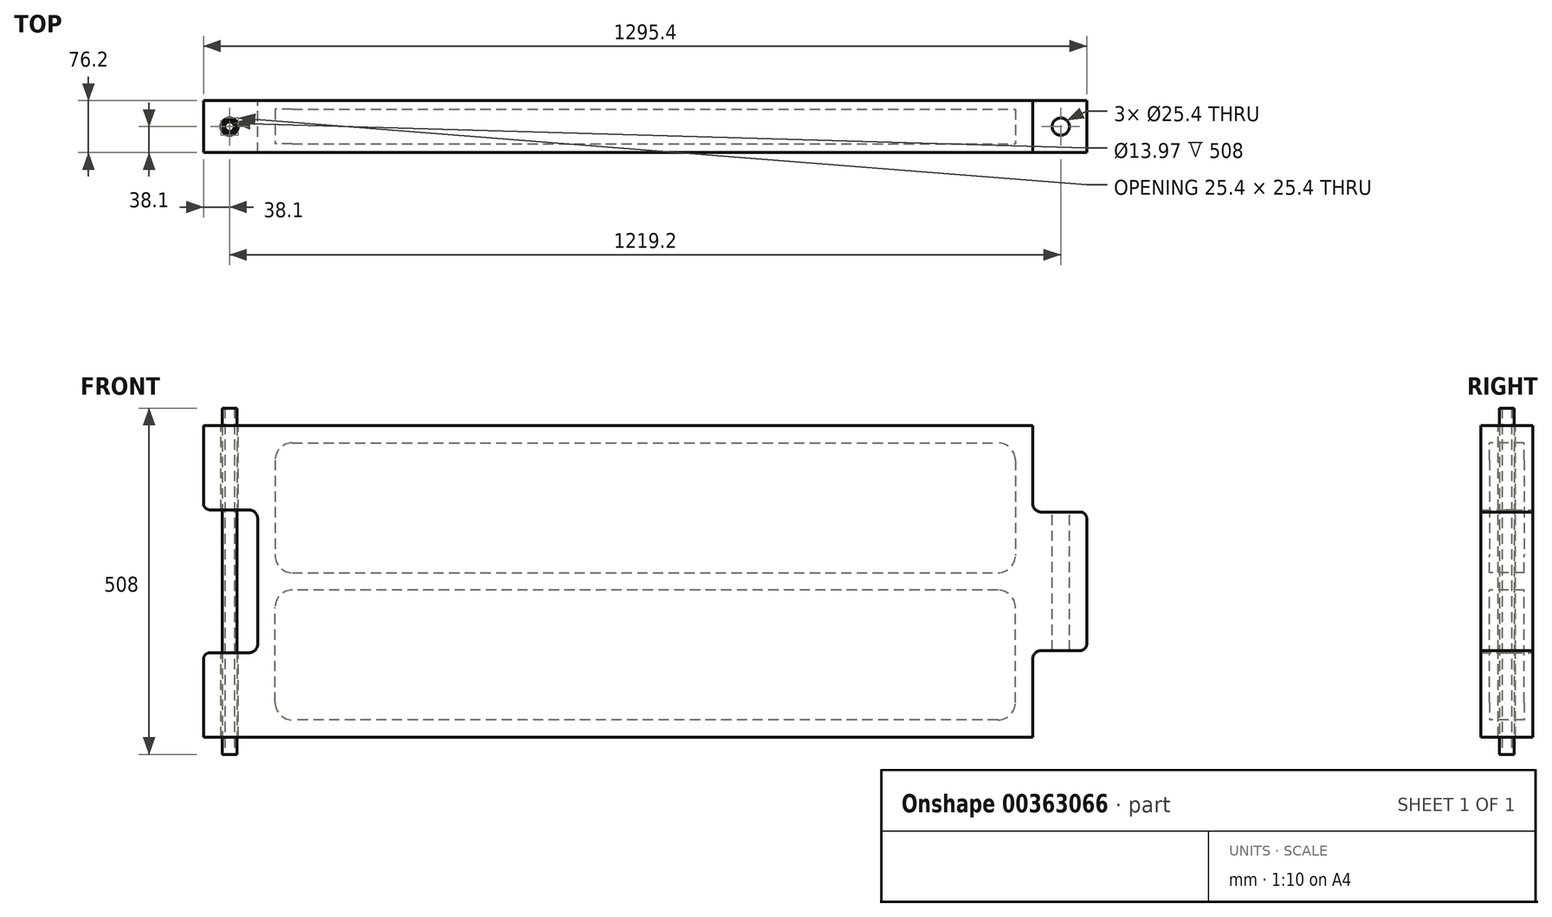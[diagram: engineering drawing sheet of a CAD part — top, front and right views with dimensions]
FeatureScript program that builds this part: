
annotation { "Feature Type Name" : "Feature", "Feature Type Description" : "" }
export const myFeature = defineFeature(function(context is Context, id is Id, definition is map)
    precondition{}
    {
        {
            var Q0;
            Q0=qCreatedBy(makeId("Front.planeOp"),FACE);
            var sketch = newSketch(context, id + "F0", { "sketchPlane" : qUnion([Q0])});
            skLineSegment(sketch, "E0.bottom", {"start": v(-568.33, 228.6) * mm, "end": v(568.32, 228.6) * mm});
            skLineSegment(sketch, "E0.top", {"start": v(-568.32, -228.6) * mm, "end": v(568.33, -228.6) * mm});
            skLineSegment(sketch, "E0.left", {"start": v(-568.33, 228.6) * mm, "end": v(-568.32, -228.6) * mm});
            skLineSegment(sketch, "E0.right", {"start": v(568.32, 228.6) * mm, "end": v(568.33, -228.6) * mm});
            skPoint(sketch, "E0.middle", {"position": v(0, 0) * mm});
            skLineSegment(sketch, "E1", {"start": v(-568.33, 228.6) * mm, "end": v(-647.7, 228.6) * mm});
            skLineSegment(sketch, "E2", {"start": v(-647.7, 228.6) * mm, "end": v(-647.7, 104.77) * mm});
            skLineSegment(sketch, "E3", {"start": v(-647.7, 104.77) * mm, "end": v(-568.32, 104.77) * mm});
            skLineSegment(sketch, "E4", {"start": v(-568.32, -228.6) * mm, "end": v(-647.7, -228.6) * mm});
            skLineSegment(sketch, "E5", {"start": v(-647.7, -228.6) * mm, "end": v(-647.7, -104.78) * mm});
            skLineSegment(sketch, "E6", {"start": v(-647.7, -104.78) * mm, "end": v(-568.32, -104.78) * mm});
            skLineSegment(sketch, "E7", {"start": v(568.32, 101.6) * mm, "end": v(647.7, 101.6) * mm});
            skLineSegment(sketch, "E8", {"start": v(647.7, 101.6) * mm, "end": v(647.7, -101.6) * mm});
            skLineSegment(sketch, "E9", {"start": v(647.7, -101.6) * mm, "end": v(568.32, -101.6) * mm});
            skPoint(sketch, "E10", {"position": v(647.7, 0) * mm});
            skSolve(sketch);
        }
        {
            var Q0;
            Q0=qSketchRegion(id+"F0",true);
            extrude(context, id + "F1", {"entities" : qUnion([Q0]), "endBound" : BoundingType.SYMMETRIC, "depth" : 76.2 * mm, "hasSecondDirection" : true, "secondDirectionOppositeDirection" : true, "secondDirectionDepth" : 36.5 * mm, "offsetDistance" : 25.4 * mm});
        }
        {
            var Q0;
            Q0=qCreatedBy(makeId("Top.planeOp"),FACE);
            var sketch = newSketch(context, id + "F2", { "sketchPlane" : qUnion([Q0])});
            skCircle(sketch, "E11", {"center": v(-609.6, 0) * mm, "radius": 12.7 * mm});
            skCircle(sketch, "E12", {"center": v(609.6, 0) * mm, "radius": 12.7 * mm});
            skLineSegment(sketch, "E13", {"start": v(-609.6, 0) * mm, "end": v(609.6, 0) * mm, "construction": true});
            skPoint(sketch, "E14", {"position": v(0, 0) * mm});
            skSolve(sketch);
        }
        {
            var Q0;
            Q0=qSketchRegion(id+"F2",true);
            extrude(context, id + "F3", {"entities" : qUnion([Q0]), "operationType" : NewBodyOperationType.REMOVE, "endBound" : BoundingType.SYMMETRIC, "oppositeDirection" : true, "depth" : 508 * mm});
        }
        {
            var Q0;
            Q0=makeQuery(id+"F1.opExtrude","SWEPT_EDGE",EDGE,{"disambiguationData":[OSD([sQuery(id+"F0.wireOp",EDGE,"E7"),sQuery(id+"F0.wireOp",EDGE,"E8")])]});
            var Q1;
            Q1=makeQuery(id+"F1.opExtrude","SWEPT_EDGE",EDGE,{"disambiguationData":[OSD([sQuery(id+"F0.wireOp",EDGE,"E8"),sQuery(id+"F0.wireOp",EDGE,"E9")])]});
            var Q2;
            Q2=makeQuery(id+"F1.opExtrude","SWEPT_EDGE",EDGE,{"disambiguationData":[OSD([sQuery(id+"F0.wireOp",EDGE,"E2"),sQuery(id+"F0.wireOp",EDGE,"E3")])]});
            var Q3;
            Q3=makeQuery(id+"F1.opExtrude","SWEPT_EDGE",EDGE,{"disambiguationData":[OSD([sQuery(id+"F0.wireOp",EDGE,"E5"),sQuery(id+"F0.wireOp",EDGE,"E6")])]});
            fillet(context, id + "F4", {"entities" : qUnion([Q0, Q1, Q2, Q3]), "radius" : 9.52 * mm, "tangentPropagation" : true, "allowEdgeOverflow" : false});
        }
        {
            var Q0;
            Q0=makeQuery(id+"F1.opExtrude","SWEPT_EDGE",EDGE,{"disambiguationData":[OSD([sQuery(id+"F0.wireOp",EDGE,"E0.left"),sQuery(id+"F0.wireOp",EDGE,"E3")])]});
            var Q1;
            Q1=makeQuery(id+"F1.opExtrude","SWEPT_EDGE",EDGE,{"disambiguationData":[OSD([sQuery(id+"F0.wireOp",EDGE,"E0.left"),sQuery(id+"F0.wireOp",EDGE,"E6")])]});
            var Q2;
            Q2=makeQuery(id+"F1.opExtrude","SWEPT_EDGE",EDGE,{"disambiguationData":[OSD([sQuery(id+"F0.wireOp",EDGE,"E0.right"),sQuery(id+"F0.wireOp",EDGE,"E9")])]});
            var Q3;
            Q3=makeQuery(id+"F1.opExtrude","SWEPT_EDGE",EDGE,{"disambiguationData":[OSD([sQuery(id+"F0.wireOp",EDGE,"E0.right"),sQuery(id+"F0.wireOp",EDGE,"E7")])]});
            fillet(context, id + "F5", {"entities" : qUnion([Q0, Q1, Q2, Q3]), "radius" : 12.7 * mm, "tangentPropagation" : true, "allowEdgeOverflow" : false});
        }
        {
            var Q0;
            Q0=qCreatedBy(makeId("Front.planeOp"),FACE);
            var sketch = newSketch(context, id + "F6", { "sketchPlane" : qUnion([Q0])});
            skPoint(sketch, "E15.middle", {"position": v(0, 0) * mm});
            skLineSegment(sketch, "E16.bottom", {"start": v(-517.52, 203.2) * mm, "end": v(-38.1, 203.2) * mm});
            skLineSegment(sketch, "E16.top", {"start": v(-517.52, 12.7) * mm, "end": v(-38.1, 12.7) * mm});
            skLineSegment(sketch, "E16.left", {"start": v(-542.92, 177.8) * mm, "end": v(-542.92, 38.1) * mm});
            skLineSegment(sketch, "E16.right", {"start": v(-12.7, 177.8) * mm, "end": v(-12.7, 38.1) * mm});
            skLineSegment(sketch, "E17", {"start": v(0, 0) * mm, "end": v(0, 71.22) * mm, "construction": true});
            skLineSegment(sketch, "E18", {"start": v(0, 0) * mm, "end": v(-136.97, 0) * mm, "construction": true});
            skPoint(sketch, "E19.visualSharp", {"position": v(-12.7, 12.7) * mm});
            skArc(sketch, "E19.filletArc", {"start": v(-38.1, 12.7) * mm, "mid": v(-20.14, 20.14) * mm, "end": v(-12.7, 38.1) * mm});
            skPoint(sketch, "E20.visualSharp", {"position": v(-12.7, 203.2) * mm});
            skArc(sketch, "E20.filletArc", {"start": v(-12.7, 177.8) * mm, "mid": v(-20.14, 195.76) * mm, "end": v(-38.1, 203.2) * mm});
            skPoint(sketch, "E21.visualSharp", {"position": v(-542.92, 203.2) * mm});
            skArc(sketch, "E21.filletArc", {"start": v(-517.52, 203.2) * mm, "mid": v(-535.49, 195.76) * mm, "end": v(-542.92, 177.8) * mm});
            skPoint(sketch, "E22.visualSharp", {"position": v(-542.92, 12.7) * mm});
            skArc(sketch, "E22.filletArc", {"start": v(-542.92, 38.1) * mm, "mid": v(-535.49, 20.14) * mm, "end": v(-517.52, 12.7) * mm});
            skLineSegment(sketch, "E23.MirrorCS", {"start": v(12.7, 177.8) * mm, "end": v(12.7, 38.1) * mm});
            skPoint(sketch, "E24.MirrorP", {"position": v(12.7, 203.2) * mm});
            skArc(sketch, "E25.MirrorCS", {"start": v(12.7, 177.8) * mm, "mid": v(20.14, 195.76) * mm, "end": v(38.1, 203.2) * mm});
            skLineSegment(sketch, "E26.MirrorCS", {"start": v(517.52, 203.2) * mm, "end": v(38.1, 203.2) * mm});
            skPoint(sketch, "E27.MirrorP", {"position": v(542.92, 203.2) * mm});
            skArc(sketch, "E28.MirrorCS", {"start": v(517.52, 203.2) * mm, "mid": v(535.49, 195.76) * mm, "end": v(542.92, 177.8) * mm});
            skLineSegment(sketch, "E29.MirrorCS", {"start": v(542.92, 177.8) * mm, "end": v(542.92, 38.1) * mm});
            skArc(sketch, "E30.MirrorCS", {"start": v(542.92, 38.1) * mm, "mid": v(535.49, 20.14) * mm, "end": v(517.52, 12.7) * mm});
            skPoint(sketch, "E31.MirrorP", {"position": v(542.92, 12.7) * mm});
            skLineSegment(sketch, "E32.MirrorCS", {"start": v(517.52, 12.7) * mm, "end": v(38.1, 12.7) * mm});
            skPoint(sketch, "E33.MirrorP", {"position": v(12.7, 12.7) * mm});
            skArc(sketch, "E34.MirrorCS", {"start": v(38.1, 12.7) * mm, "mid": v(20.14, 20.14) * mm, "end": v(12.7, 38.1) * mm});
            skArc(sketch, "E35.MirrorCS", {"start": v(38.1, -12.7) * mm, "mid": v(20.14, -20.14) * mm, "end": v(12.7, -38.1) * mm});
            skArc(sketch, "E36.MirrorCS", {"start": v(542.92, -38.1) * mm, "mid": v(535.49, -20.14) * mm, "end": v(517.52, -12.7) * mm});
            skArc(sketch, "E37.MirrorCS", {"start": v(-517.52, -203.2) * mm, "mid": v(-535.49, -195.76) * mm, "end": v(-542.92, -177.8) * mm});
            skArc(sketch, "E38.MirrorCS", {"start": v(-38.1, -12.7) * mm, "mid": v(-20.14, -20.14) * mm, "end": v(-12.7, -38.1) * mm});
            skPoint(sketch, "E39.MirrorP", {"position": v(12.7, -12.7) * mm});
            skArc(sketch, "E40.MirrorCS", {"start": v(-542.92, -38.1) * mm, "mid": v(-535.49, -20.14) * mm, "end": v(-517.52, -12.7) * mm});
            skArc(sketch, "E41.MirrorCS", {"start": v(517.52, -203.2) * mm, "mid": v(535.49, -195.76) * mm, "end": v(542.92, -177.8) * mm});
            skArc(sketch, "E42.MirrorCS", {"start": v(-12.7, -177.8) * mm, "mid": v(-20.14, -195.76) * mm, "end": v(-38.1, -203.2) * mm});
            skArc(sketch, "E43.MirrorCS", {"start": v(12.7, -177.8) * mm, "mid": v(20.14, -195.76) * mm, "end": v(38.1, -203.2) * mm});
            skLineSegment(sketch, "E44.MirrorCS", {"start": v(0, 0) * mm, "end": v(0, -71.22) * mm, "construction": true});
            skPoint(sketch, "E45.MirrorP", {"position": v(542.92, -12.7) * mm});
            skPoint(sketch, "E46.MirrorP", {"position": v(-12.7, -12.7) * mm});
            skLineSegment(sketch, "E47.MirrorCS", {"start": v(-517.52, -203.2) * mm, "end": v(-38.1, -203.2) * mm});
            skPoint(sketch, "E48.MirrorP", {"position": v(12.7, -203.2) * mm});
            skPoint(sketch, "E49.MirrorP", {"position": v(-542.92, -12.7) * mm});
            skPoint(sketch, "E50.MirrorP", {"position": v(-542.92, -203.2) * mm});
            skLineSegment(sketch, "E51.MirrorCS", {"start": v(542.92, -177.8) * mm, "end": v(542.92, -38.1) * mm});
            skPoint(sketch, "E52.MirrorP", {"position": v(542.92, -203.2) * mm});
            skLineSegment(sketch, "E53.MirrorCS", {"start": v(12.7, -177.8) * mm, "end": v(12.7, -38.1) * mm});
            skLineSegment(sketch, "E54.MirrorCS", {"start": v(-542.92, -177.8) * mm, "end": v(-542.92, -38.1) * mm});
            skLineSegment(sketch, "E55.MirrorCS", {"start": v(517.52, -203.2) * mm, "end": v(38.1, -203.2) * mm});
            skLineSegment(sketch, "E56.MirrorCS", {"start": v(517.52, -12.7) * mm, "end": v(38.1, -12.7) * mm});
            skPoint(sketch, "E57.MirrorP", {"position": v(-12.7, -203.2) * mm});
            skLineSegment(sketch, "E58.MirrorCS", {"start": v(-517.52, -12.7) * mm, "end": v(-38.1, -12.7) * mm});
            skLineSegment(sketch, "E59.MirrorCS", {"start": v(-12.7, -177.8) * mm, "end": v(-12.7, -38.1) * mm});
            skLineSegment(sketch, "E60", {"start": v(-38.1, 203.2) * mm, "end": v(38.1, 203.2) * mm});
            skLineSegment(sketch, "E61", {"start": v(-38.1, 12.7) * mm, "end": v(38.1, 12.7) * mm});
            skLineSegment(sketch, "E62", {"start": v(-38.1, -12.7) * mm, "end": v(38.1, -12.7) * mm});
            skLineSegment(sketch, "E63", {"start": v(-38.1, -203.2) * mm, "end": v(38.1, -203.2) * mm});
            skSolve(sketch);
        }
        {
            var Q0;
            Q0=qSketchRegion(id+"F6",true);
            extrude(context, id + "F7", {"entities" : qUnion([Q0]), "operationType" : NewBodyOperationType.REMOVE, "endBound" : BoundingType.SYMMETRIC, "oppositeDirection" : true, "depth" : 50.8 * mm, "offsetDistance" : 25.4 * mm});
        }
        {
            var Q0;
            Q0=qCreatedBy(makeId("Top.planeOp"),FACE);
            var sketch = newSketch(context, id + "F8", { "sketchPlane" : qUnion([Q0])});
            skCircle(sketch, "E64", {"center": v(-609.6, 0) * mm, "radius": 10.67 * mm});
            skCircle(sketch, "E65.0", {"center": v(-609.6, 0) * mm, "radius": 12.7 * mm});
            skCircle(sketch, "E66", {"center": v(-609.6, 0) * mm, "radius": 6.99 * mm});
            skSolve(sketch);
        }
        {
            var Q0;
            Q0=makeQuery(id+"F8.imprint","IMPRINT",FACE,{"disambiguationData":[TD([[makeQuery(id+"F8.imprint","IMPRINT",EDGE,{"derivedFrom":sQuery(id+"F8.wireOp",EDGE,"E64")}),1.0]])]});
            extrude(context, id + "F9", {"entities" : qUnion([Q0]), "endBound" : BoundingType.SYMMETRIC, "depth" : 508 * mm});
        }
    });
